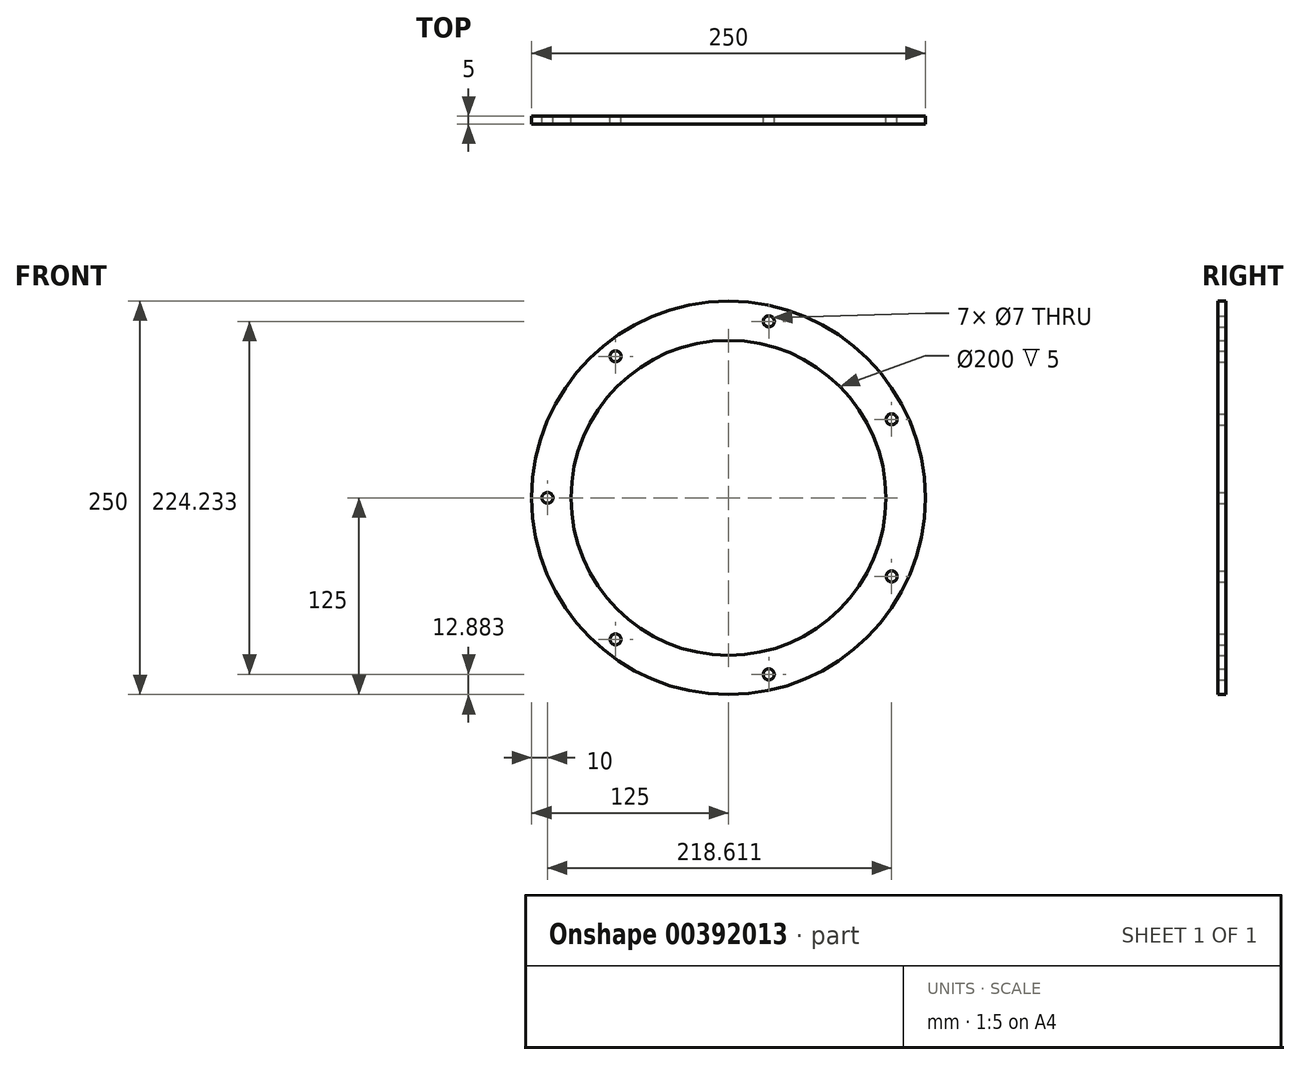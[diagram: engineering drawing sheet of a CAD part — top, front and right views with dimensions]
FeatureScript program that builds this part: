
annotation { "Feature Type Name" : "Feature", "Feature Type Description" : "" }
export const myFeature = defineFeature(function(context is Context, id is Id, definition is map)
    precondition{}
    {
        {
            var Q0;
            Q0=qCreatedBy(makeId("Front.planeOp"),FACE);
            var sketch = newSketch(context, id + "F0", { "sketchPlane" : qUnion([Q0])});
            skCircle(sketch, "E0", {"center": v(0, 0) * mm, "radius": 125 * mm});
            skArc(sketch, "E1", {"start": v(-7.37, 99.73) * mm, "mid": v(-70.71, 70.71) * mm, "end": v(-99.73, 7.37) * mm});
            skCircle(sketch, "E2", {"center": v(0, 0) * mm, "radius": 115 * mm, "construction": true});
            skCircle(sketch, "E3", {"center": v(-115, 0) * mm, "radius": 3.5 * mm});
            skCircle(sketch, "E4.1.0", {"center": v(-71.7, -89.91) * mm, "radius": 3.5 * mm});
            skCircle(sketch, "E4.2.0", {"center": v(25.59, -112.12) * mm, "radius": 3.5 * mm});
            skCircle(sketch, "E4.3.0", {"center": v(103.61, -49.9) * mm, "radius": 3.5 * mm});
            skCircle(sketch, "E4.4.0", {"center": v(103.61, 49.9) * mm, "radius": 3.5 * mm});
            skCircle(sketch, "E4.5.0", {"center": v(25.59, 112.12) * mm, "radius": 3.5 * mm});
            skLineSegment(sketch, "E5.left", {"start": v(2, 94.74) * mm, "end": v(2, 64.62) * mm});
            skLineSegment(sketch, "E5.right", {"start": v(-2, 94.74) * mm, "end": v(-2, 64.62) * mm});
            skLineSegment(sketch, "E6.bottom", {"start": v(-94.74, 2) * mm, "end": v(-64.62, 2) * mm});
            skLineSegment(sketch, "E6.top", {"start": v(-94.74, -2) * mm, "end": v(-64.62, -2) * mm});
            skPoint(sketch, "E7.orphan", {"position": v(-2, 105.37) * mm});
            skPoint(sketch, "E8.orphan", {"position": v(2, 105.37) * mm});
            skPoint(sketch, "E6.left.end.orphan", {"position": v(-105.96, -2) * mm});
            skPoint(sketch, "E6.left.start.orphan", {"position": v(-105.96, 2) * mm});
            skPoint(sketch, "E6.right.start.orphan", {"position": v(105.96, 2) * mm});
            skPoint(sketch, "E9.orphan", {"position": v(105.96, -2) * mm});
            skPoint(sketch, "E5.top.end.orphan", {"position": v(-2, -105.37) * mm});
            skPoint(sketch, "E5.top.start.orphan", {"position": v(2, -105.37) * mm});
            skPoint(sketch, "E10.visualSharp", {"position": v(-2, 99.98) * mm});
            skArc(sketch, "E10.filletArc", {"start": v(-2, 94.74) * mm, "mid": v(-3.6, 98.4) * mm, "end": v(-7.37, 99.73) * mm});
            skPoint(sketch, "E11.visualSharp", {"position": v(2, 99.98) * mm});
            skArc(sketch, "E11.filletArc", {"start": v(7.37, 99.73) * mm, "mid": v(3.6, 98.4) * mm, "end": v(2, 94.74) * mm});
            skArc(sketch, "E12.trimOffspring", {"start": v(-99.73, -7.37) * mm, "mid": v(-70.71, -70.71) * mm, "end": v(-7.37, -99.73) * mm});
            skLineSegment(sketch, "E13.trimOffspring", {"start": v(-2, -7) * mm, "end": v(-2, -49.5) * mm});
            skLineSegment(sketch, "E14.trimOffspring", {"start": v(2, -7) * mm, "end": v(2, -49.5) * mm});
            skLineSegment(sketch, "E15.trimOffspring", {"start": v(7, 2) * mm, "end": v(49.5, 2) * mm});
            skLineSegment(sketch, "E16.trimOffspring", {"start": v(7, -2) * mm, "end": v(49.5, -2) * mm});
            skArc(sketch, "E17.trimOffspring", {"start": v(99.73, 7.37) * mm, "mid": v(70.71, 70.71) * mm, "end": v(7.37, 99.73) * mm});
            skArc(sketch, "E18.trimOffspring", {"start": v(7.37, -99.73) * mm, "mid": v(70.71, -70.71) * mm, "end": v(99.73, -7.37) * mm});
            skPoint(sketch, "E19.visualSharp", {"position": v(-99.98, 2) * mm});
            skArc(sketch, "E19.filletArc", {"start": v(-99.73, 7.37) * mm, "mid": v(-98.4, 3.6) * mm, "end": v(-94.74, 2) * mm});
            skPoint(sketch, "E20.visualSharp", {"position": v(-99.98, -2) * mm});
            skArc(sketch, "E20.filletArc", {"start": v(-94.74, -2) * mm, "mid": v(-98.4, -3.6) * mm, "end": v(-99.73, -7.37) * mm});
            skPoint(sketch, "E21.visualSharp", {"position": v(-2, -2) * mm});
            skArc(sketch, "E21.filletArc", {"start": v(-2, -7) * mm, "mid": v(-3.46, -3.46) * mm, "end": v(-7, -2) * mm});
            skPoint(sketch, "E22.visualSharp", {"position": v(-2, 2) * mm});
            skArc(sketch, "E22.filletArc", {"start": v(-7, 2) * mm, "mid": v(-3.46, 3.46) * mm, "end": v(-2, 7) * mm});
            skPoint(sketch, "E23.visualSharp", {"position": v(2, 2) * mm});
            skArc(sketch, "E23.filletArc", {"start": v(2, 7) * mm, "mid": v(3.46, 3.46) * mm, "end": v(7, 2) * mm});
            skPoint(sketch, "E24.visualSharp", {"position": v(2, -2) * mm});
            skArc(sketch, "E24.filletArc", {"start": v(7, -2) * mm, "mid": v(3.46, -3.46) * mm, "end": v(2, -7) * mm});
            skPoint(sketch, "E25.visualSharp", {"position": v(99.98, -2) * mm});
            skArc(sketch, "E25.filletArc", {"start": v(99.73, -7.37) * mm, "mid": v(98.4, -3.6) * mm, "end": v(94.74, -2) * mm});
            skPoint(sketch, "E26.visualSharp", {"position": v(99.98, 2) * mm});
            skArc(sketch, "E26.filletArc", {"start": v(94.74, 2) * mm, "mid": v(98.4, 3.6) * mm, "end": v(99.73, 7.37) * mm});
            skPoint(sketch, "E27.visualSharp", {"position": v(2, -99.98) * mm});
            skArc(sketch, "E27.filletArc", {"start": v(2, -94.74) * mm, "mid": v(3.6, -98.4) * mm, "end": v(7.37, -99.73) * mm});
            skPoint(sketch, "E28.visualSharp", {"position": v(-2, -99.98) * mm});
            skArc(sketch, "E28.filletArc", {"start": v(-7.37, -99.73) * mm, "mid": v(-3.6, -98.4) * mm, "end": v(-2, -94.74) * mm});
            skArc(sketch, "E29", {"start": v(-6.46, 59.65) * mm, "mid": v(-42.43, 42.43) * mm, "end": v(-59.65, 6.46) * mm});
            skArc(sketch, "E30", {"start": v(-7.7, 54.46) * mm, "mid": v(-38.9, 38.9) * mm, "end": v(-54.46, 7.7) * mm});
            skCircle(sketch, "E31.1.6.0", {"center": v(-71.7, 89.91) * mm, "radius": 3.5 * mm});
            skLineSegment(sketch, "E32.trimOffspring", {"start": v(-2, 49.5) * mm, "end": v(-2, 7) * mm});
            skLineSegment(sketch, "E33.trimOffspring", {"start": v(2, 49.5) * mm, "end": v(2, 7) * mm});
            skLineSegment(sketch, "E34.trimOffspring", {"start": v(64.62, 2) * mm, "end": v(94.74, 2) * mm});
            skArc(sketch, "E35.trimOffspring", {"start": v(54.46, 7.7) * mm, "mid": v(38.9, 38.9) * mm, "end": v(7.7, 54.46) * mm});
            skLineSegment(sketch, "E36.trimOffspring", {"start": v(64.62, -2) * mm, "end": v(94.74, -2) * mm});
            skArc(sketch, "E37.trimOffspring", {"start": v(59.65, 6.46) * mm, "mid": v(42.43, 42.43) * mm, "end": v(6.46, 59.65) * mm});
            skArc(sketch, "E38.trimOffspring", {"start": v(6.46, -59.65) * mm, "mid": v(42.43, -42.43) * mm, "end": v(59.65, -6.46) * mm});
            skLineSegment(sketch, "E39.trimOffspring", {"start": v(-2, -64.62) * mm, "end": v(-2, -94.74) * mm});
            skArc(sketch, "E40.trimOffspring", {"start": v(7.7, -54.46) * mm, "mid": v(38.9, -38.9) * mm, "end": v(54.46, -7.7) * mm});
            skLineSegment(sketch, "E41.trimOffspring", {"start": v(2, -64.62) * mm, "end": v(2, -94.74) * mm});
            skArc(sketch, "E42.trimOffspring", {"start": v(-59.65, -6.46) * mm, "mid": v(-42.43, -42.43) * mm, "end": v(-6.46, -59.65) * mm});
            skLineSegment(sketch, "E43.trimOffspring", {"start": v(-49.5, 2) * mm, "end": v(-7, 2) * mm});
            skLineSegment(sketch, "E44.trimOffspring", {"start": v(-49.5, -2) * mm, "end": v(-7, -2) * mm});
            skArc(sketch, "E45.trimOffspring", {"start": v(-54.46, -7.7) * mm, "mid": v(-38.9, -38.9) * mm, "end": v(-7.7, -54.46) * mm});
            skPoint(sketch, "E46.visualSharp", {"position": v(-2, 59.97) * mm});
            skArc(sketch, "E46.filletArc", {"start": v(-6.46, 59.65) * mm, "mid": v(-3.28, 61.28) * mm, "end": v(-2, 64.62) * mm});
            skPoint(sketch, "E47.visualSharp", {"position": v(-2, 54.96) * mm});
            skArc(sketch, "E47.filletArc", {"start": v(-2, 49.5) * mm, "mid": v(-3.72, 53.28) * mm, "end": v(-7.7, 54.46) * mm});
            skPoint(sketch, "E48.visualSharp", {"position": v(2, 59.97) * mm});
            skArc(sketch, "E48.filletArc", {"start": v(2, 64.62) * mm, "mid": v(3.28, 61.28) * mm, "end": v(6.46, 59.65) * mm});
            skPoint(sketch, "E49.visualSharp", {"position": v(2, 54.96) * mm});
            skArc(sketch, "E49.filletArc", {"start": v(7.7, 54.46) * mm, "mid": v(3.72, 53.28) * mm, "end": v(2, 49.5) * mm});
            skPoint(sketch, "E50.visualSharp", {"position": v(-59.97, 2) * mm});
            skArc(sketch, "E50.filletArc", {"start": v(-64.62, 2) * mm, "mid": v(-61.28, 3.28) * mm, "end": v(-59.65, 6.46) * mm});
            skPoint(sketch, "E51.visualSharp", {"position": v(-54.96, 2) * mm});
            skArc(sketch, "E51.filletArc", {"start": v(-54.46, 7.7) * mm, "mid": v(-53.28, 3.72) * mm, "end": v(-49.5, 2) * mm});
            skPoint(sketch, "E52.visualSharp", {"position": v(-54.96, -2) * mm});
            skArc(sketch, "E52.filletArc", {"start": v(-49.5, -2) * mm, "mid": v(-53.28, -3.72) * mm, "end": v(-54.46, -7.7) * mm});
            skPoint(sketch, "E53.visualSharp", {"position": v(-59.97, -2) * mm});
            skArc(sketch, "E53.filletArc", {"start": v(-59.65, -6.46) * mm, "mid": v(-61.28, -3.28) * mm, "end": v(-64.62, -2) * mm});
            skPoint(sketch, "E54.visualSharp", {"position": v(54.96, -2) * mm});
            skArc(sketch, "E54.filletArc", {"start": v(54.46, -7.7) * mm, "mid": v(53.28, -3.72) * mm, "end": v(49.5, -2) * mm});
            skPoint(sketch, "E55.visualSharp", {"position": v(59.97, -2) * mm});
            skArc(sketch, "E55.filletArc", {"start": v(64.62, -2) * mm, "mid": v(61.28, -3.28) * mm, "end": v(59.65, -6.46) * mm});
            skPoint(sketch, "E56.visualSharp", {"position": v(59.97, 2) * mm});
            skArc(sketch, "E56.filletArc", {"start": v(59.65, 6.46) * mm, "mid": v(61.28, 3.28) * mm, "end": v(64.62, 2) * mm});
            skPoint(sketch, "E57.visualSharp", {"position": v(54.96, 2) * mm});
            skArc(sketch, "E57.filletArc", {"start": v(49.5, 2) * mm, "mid": v(53.28, 3.72) * mm, "end": v(54.46, 7.7) * mm});
            skPoint(sketch, "E58.visualSharp", {"position": v(2, -59.97) * mm});
            skArc(sketch, "E58.filletArc", {"start": v(6.46, -59.65) * mm, "mid": v(3.28, -61.28) * mm, "end": v(2, -64.62) * mm});
            skPoint(sketch, "E59.visualSharp", {"position": v(2, -54.96) * mm});
            skArc(sketch, "E59.filletArc", {"start": v(2, -49.5) * mm, "mid": v(3.72, -53.28) * mm, "end": v(7.7, -54.46) * mm});
            skPoint(sketch, "E60.visualSharp", {"position": v(-2, -54.96) * mm});
            skArc(sketch, "E60.filletArc", {"start": v(-7.7, -54.46) * mm, "mid": v(-3.72, -53.28) * mm, "end": v(-2, -49.5) * mm});
            skPoint(sketch, "E61.visualSharp", {"position": v(-2, -59.97) * mm});
            skArc(sketch, "E61.filletArc", {"start": v(-2, -64.62) * mm, "mid": v(-3.28, -61.28) * mm, "end": v(-6.46, -59.65) * mm});
            skCircle(sketch, "E62", {"center": v(0, 0) * mm, "radius": 100 * mm});
            skSolve(sketch);
        }
        {
            var Q0;
            Q0=makeQuery(id+"F0.imprint","IMPRINT",FACE,{"disambiguationData":[TD([[makeQuery(id+"F0.imprint","IMPRINT",EDGE,{"derivedFrom":sQuery(id+"F0.wireOp",EDGE,"E0")}),1.0]])]});
            extrude(context, id + "F1", {"entities" : qUnion([Q0]), "depth" : 5 * mm});
        }
    });
